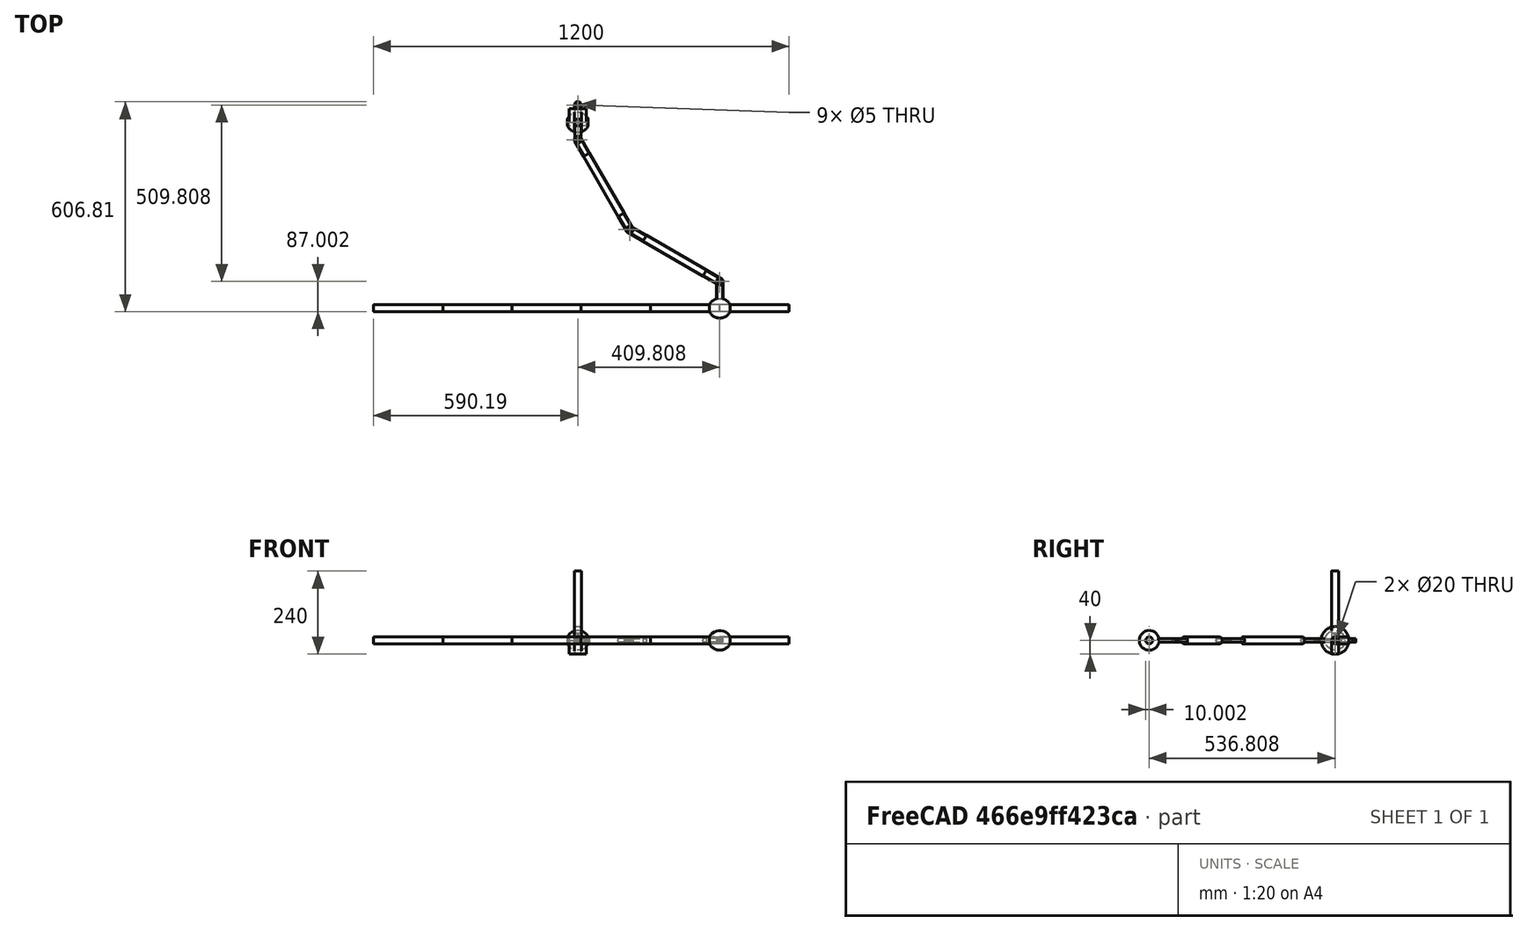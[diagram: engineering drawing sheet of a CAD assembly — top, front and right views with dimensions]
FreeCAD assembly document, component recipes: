
FREECAD ASSEMBLY — COMPONENT RECIPES ("Demo7Rigid")

This assembly document has 7 components, labeled P0..P6 below (a component is one placed body or linked part). 7 of them carry a construction recipe — the FreeCAD feature program that regenerates the part from scratch, quoted from this document or its linked companion documents; the rest are supplied as boundary geometry only. No exploded tour is included for this assembly.
COMPONENT P0 — recipe-attached ("Weight", modeled in this document).
Construction recipe (the document's own serialized feature program — sketch geometry with constraints, then the solid features built on it; lengths are millimeters unless a unit is written):

FEATURE [Sketcher::SketchObject] Sketch
  FullyConstrained = true
  MapMode = 5
  Support = -> [XY_Plane]
  sketch-geometry (2):
    g0: LineSegment StartX=-30 StartY=10 StartZ=0 EndX=30 EndY=10 EndZ=0
    g1: ArcOfCircle CenterX=0 CenterY=-5 CenterZ=0 NormalX=0 NormalY=0 NormalZ=1 AngleXU=0 Radius=33.541 StartAngle=0.463648 EndAngle=2.67795
  constraints (7):
    c: Horizontal(g0)
    c: DistanceY(g-1,g0) = 10
    c: DistanceX(g-1,g0) = 30
    c: PointOnObject(g1,g-2)
    c: DistanceY(g1,g-1) = 5
    c: Coincident(g1,g0)
    c: Coincident(g1,g0)
FEATURE [PartDesign::Revolution] Revolution
  Angle = 360
  Axis = (1,0,0)
  Base = (0,0,0)
  Profile = -> Sketch
  ReferenceAxis = -> Sketch [H_Axis]
FEATURE [PartDesign::CoordinateSystem] WeightTop
  AttacherType = Attacher::AttachEngine3D
  MapMode = 11
  Placement = pos=(30,-1.8e-15,0) rot=(0.707107,0,0.707107;3.14159rad)
  Support = -> [Revolution]
FEATURE [PartDesign::CoordinateSystem] WeightBot
  AttacherType = Attacher::AttachEngine3D
  MapMode = 11
  Placement = pos=(-30,0,0) rot=(0.707107,0,0.707107;3.14159rad)
  Support = -> [Revolution]
FEATURE [PartDesign::CoordinateSystem] WeightLCS
  AttacherType = Attacher::AttachEngine3D
  MapMode = 2
  Support = -> [Body003]
FEATURE [PartDesign::Body] Body  label="Weight"
  Group = -> [Sketch,Revolution,WeightLCS,WeightTop,WeightBot]
  Origin = -> Origin
  Tip = -> Revolution
COMPONENT P1 — recipe-attached ("Rod", modeled in this document).
Construction recipe (the document's own serialized feature program — sketch geometry with constraints, then the solid features built on it; lengths are millimeters unless a unit is written):

FEATURE [Sketcher::SketchObject] Sketch001
  FullyConstrained = true
  MapMode = 5
  Support = -> [XY_Plane001]
  sketch-geometry (1):
    g0: Circle CenterX=0 CenterY=0 CenterZ=0 NormalX=0 NormalY=0 NormalZ=1 AngleXU=0 Radius=10
  constraints (2):
    c: Coincident(g0,g-1)
    c: Diameter(g0) = 20
FEATURE [PartDesign::Pad] Pad
  Direction = (0,0,1)
  Length = 200
  Length2 = 10
  Profile = -> Sketch001
  ReferenceAxis = -> Sketch001 [N_Axis]
  Type = 0
FEATURE [PartDesign::CoordinateSystem] RodTop
  AttacherType = Attacher::AttachEngine3D
  MapMode = 11
  Placement = pos=(0,0,200) rot=(0,0,1;1.5708rad)
  Support = -> [Pad]
FEATURE [PartDesign::CoordinateSystem] RodBottom
  AttacherType = Attacher::AttachEngine3D
  MapMode = 11
  Placement = pos=(0,0,0) rot=(0,0,1;1.5708rad)
  Support = -> [Pad]
FEATURE [PartDesign::Body] Body001  label="Rod"
  Group = -> [Sketch001,Pad,RodTop,RodBottom]
  Origin = -> Origin001
  Tip = -> Pad
COMPONENT P2 — recipe-attached ("LugBody", modeled in this document).
Construction recipe (the document's own serialized feature program — sketch geometry with constraints, then the solid features built on it; lengths are millimeters unless a unit is written):

FEATURE [Sketcher::SketchObject] Sketch002
  FullyConstrained = true
  MapMode = 5
  Support = -> [XY_Plane002]
  sketch-geometry (5):
    g0: LineSegment StartX=-10 StartY=0 StartZ=0 EndX=-10 EndY=50 EndZ=0
    g1: ArcOfCircle CenterX=0 CenterY=50 CenterZ=0 NormalX=0 NormalY=0 NormalZ=1 AngleXU=0 Radius=10 StartAngle=1e-16 EndAngle=3.14159
    g2: LineSegment StartX=10 StartY=50 StartZ=0 EndX=10 EndY=0 EndZ=0
    g3: LineSegment StartX=10 StartY=0 StartZ=0 EndX=-10 EndY=0 EndZ=0
    g4: Circle CenterX=0 CenterY=50 CenterZ=0 NormalX=0 NormalY=0 NormalZ=1 AngleXU=0 Radius=2.5
  constraints (13):
    c: PointOnObject(g0,g-1)
    c: Vertical(g0)
    c: Tangent(g0,g1) = 1.5708
    c: Tangent(g1,g2) = 1.5708
    c: Coincident(g2,g3)
    c: Coincident(g3,g0)
    c: Horizontal(g3)
    c: PointOnObject(g1,g-2)
    c: Vertical(g2)
    c: Diameter(g1) = 20
    c: Distance(g2) = 50
    c: Coincident(g4,g1)
    c: Diameter(g4) = 5
FEATURE [PartDesign::Pad] Pad001
  Direction = (0,0,1)
  Length = 10
  Length2 = 10
  Midplane = true
  Profile = -> Sketch002
  ReferenceAxis = -> Sketch002 [N_Axis]
  Type = 0
FEATURE [PartDesign::Body] Body002  label="LugBody"
  Group = -> [Sketch002,Pad001]
  Origin = -> Origin002
  Tip = -> Pad001
COMPONENT P3 — recipe-attached ("LugCylinder", modeled in this document).
Construction recipe (the document's own serialized feature program — sketch geometry with constraints, then the solid features built on it; lengths are millimeters unless a unit is written):

FEATURE [Sketcher::SketchObject] Sketch003
  FullyConstrained = true
  MapMode = 5
  Placement = pos=(0,0,0) rot=(1,0,0;1.5708rad)
  Support = -> [XZ_Plane003]
  sketch-geometry (1):
    g0: Circle CenterX=0 CenterY=0 CenterZ=0 NormalX=0 NormalY=0 NormalZ=1 AngleXU=0 Radius=10
  constraints (2):
    c: Coincident(g0,g-1)
    c: Diameter(g0) = 20
FEATURE [PartDesign::Pad] Pad002
  Direction = (0,-1,-2e-16)
  Length = 60
  Length2 = 10
  Placement = pos=(0,0,0) rot=(1,0,0;1.5708rad)
  Profile = -> Sketch003
  ReferenceAxis = -> Sketch003 [N_Axis]
  Reversed = true
  Type = 0
FEATURE [PartDesign::Boolean] Boolean
  BaseFeature = -> Pad002
  Group = -> [Body002]
  Type = 2
FEATURE [PartDesign::CoordinateSystem] LugHole
  AttacherType = Attacher::AttachEngine3D
  MapMode = 11
  Placement = pos=(0,50,5) rot=(0,0,1;1.5708rad)
  Support = -> [Boolean]
FEATURE [PartDesign::CoordinateSystem] LugFace
  AttacherType = Attacher::AttachEngine3D
  MapMode = 5
  Placement = pos=(0,0,0) rot=(1,0,0;1.5708rad)
  Support = -> [Boolean]
FEATURE [PartDesign::CoordinateSystem] LugRot30
  AttacherType = Attacher::AttachEngine3D
  AttachmentOffset = pos=(0,0,0) rot=(0,0,1;0.523599rad)
  MapMode = 11
  Placement = pos=(0,50,5) rot=(0,0,1;2.0944rad)
  Support = -> [Boolean]
FEATURE [PartDesign::CoordinateSystem] LugRot60
  AttacherType = Attacher::AttachEngine3D
  AttachmentOffset = pos=(0,0,0) rot=(0,0,1;1.0472rad)
  MapMode = 11
  Placement = pos=(0,50,5) rot=(0,0,1;2.61799rad)
  Support = -> [Boolean]
FEATURE [PartDesign::Body] Body003  label="LugCylinder"
  Group = -> [Sketch003,Pad002,Boolean,LugHole,LugFace,LugRot30,LugRot60]
  Origin = -> Origin003
  Tip = -> Boolean
COMPONENT P4 — recipe-attached ("BobBody", modeled in this document).
Construction recipe (the document's own serialized feature program — sketch geometry with constraints, then the solid features built on it; lengths are millimeters unless a unit is written):

FEATURE [Sketcher::SketchObject] Sketch004
  FullyConstrained = true
  MapMode = 5
  Support = -> [XY_Plane004]
  sketch-geometry (4):
    g0: LineSegment StartX=-10 StartY=0 StartZ=0 EndX=-10 EndY=30 EndZ=0
    g1: ArcOfCircle CenterX=0 CenterY=30 CenterZ=0 NormalX=0 NormalY=0 NormalZ=1 AngleXU=0 Radius=10 StartAngle=2e-16 EndAngle=3.14159
    g2: LineSegment StartX=10 StartY=30 StartZ=0 EndX=10 EndY=0 EndZ=0
    g3: LineSegment StartX=10 StartY=0 StartZ=0 EndX=-10 EndY=0 EndZ=0
  constraints (11):
    c: PointOnObject(g0,g-1)
    c: Vertical(g0)
    c: Tangent(g0,g1) = 1.5708
    c: Tangent(g1,g2) = 1.5708
    c: Coincident(g2,g3)
    c: Coincident(g3,g0)
    c: Vertical(g2)
    c: PointOnObject(g1,g-2)
    c: Diameter(g1) = 20
    c: Distance(g0) = 30
    c: PointOnObject(g2,g-1)
FEATURE [PartDesign::Revolution] Revolution001
  Angle = 360
  Axis = (1,0,0)
  Base = (0,0,0)
  Profile = -> Sketch004
  ReferenceAxis = -> Sketch004 [H_Axis]
FEATURE [PartDesign::CoordinateSystem] BobBody  label="BobBody001"
  AttacherType = Attacher::AttachEngine3D
  MapMode = 11
  Placement = pos=(-10,0,0) rot=(0.707107,0,0.707107;3.14159rad)
  Support = -> [Revolution001]
FEATURE [PartDesign::Body] Body004  label="BobBody"
  Group = -> [Sketch004,Revolution001,BobBody]
  Origin = -> Origin004
  Tip = -> Revolution001
COMPONENT P5 — recipe-attached ("GroundBody", modeled in this document).
Construction recipe (the document's own serialized feature program — sketch geometry with constraints, then the solid features built on it; lengths are millimeters unless a unit is written):

FEATURE [Sketcher::SketchObject] Sketch005
  FullyConstrained = true
  MapMode = 5
  Support = -> [XY_Plane005]
  sketch-geometry (4):
    g0: LineSegment StartX=-25 StartY=10 StartZ=0 EndX=25 EndY=10 EndZ=0
    g1: LineSegment StartX=25 StartY=10 StartZ=0 EndX=25 EndY=-10 EndZ=0
    g2: LineSegment StartX=25 StartY=-10 StartZ=0 EndX=-25 EndY=-10 EndZ=0
    g3: LineSegment StartX=-25 StartY=-10 StartZ=0 EndX=-25 EndY=10 EndZ=0
  constraints (11):
    c: Coincident(g0,g1)
    c: Coincident(g1,g2)
    c: Coincident(g2,g3)
    c: Coincident(g3,g0)
    c: Horizontal(g0)
    c: Horizontal(g2)
    c: Vertical(g1)
    c: Vertical(g3)
    c: DistanceY(g2,g0) = 20
    c: DistanceX(g0,g0) = 50
    c: Symmetric(g0,g1,g-1)
FEATURE [PartDesign::Pad] Pad003
  Direction = (0,0,1)
  Length = 40
  Length2 = 10
  Profile = -> Sketch005
  ReferenceAxis = -> Sketch005 [N_Axis]
  Reversed = true
  Type = 0
FEATURE [PartDesign::CoordinateSystem] GroundLCS
  AttacherType = Attacher::AttachEngine3D
  MapMode = 5
  Placement = pos=(0,0,-40) rot=(1,0,0;3.14159rad)
  Support = -> [Pad003]
FEATURE [PartDesign::Body] Body005  label="GroundBody"
  Group = -> [Sketch005,Pad003,GroundLCS]
  Origin = -> Origin005
  Tip = -> Pad003
COMPONENT P6 — recipe-attached ("Spacer", modeled in this document).
Construction recipe (the document's own serialized feature program — sketch geometry with constraints, then the solid features built on it; lengths are millimeters unless a unit is written):

FEATURE [Sketcher::SketchObject] Sketch006
  FullyConstrained = true
  MapMode = 5
  Support = -> [XY_Plane007]
  sketch-geometry (2):
    g0: Circle CenterX=0 CenterY=0 CenterZ=0 NormalX=0 NormalY=0 NormalZ=1 AngleXU=0 Radius=10
    g1: Circle CenterX=0 CenterY=0 CenterZ=0 NormalX=0 NormalY=0 NormalZ=1 AngleXU=0 Radius=2.5
  constraints (4):
    c: Coincident(g0,g-1)
    c: Coincident(g1,g0)
    c: Diameter(g0) = 20
    c: Diameter(g1) = 5
FEATURE [PartDesign::Pad] Pad004
  Direction = (0,0,1)
  Length = 20
  Length2 = 10
  Profile = -> Sketch006
  ReferenceAxis = -> Sketch006 [N_Axis]
  Type = 0
FEATURE [PartDesign::CoordinateSystem] SpacerTop
  AttacherType = Attacher::AttachEngine3D
  MapMode = 11
  Placement = pos=(0,0,20) rot=(0,0,1;1.5708rad)
  Support = -> [Pad004]
FEATURE [PartDesign::Body] Body006  label="Spacer"
  Group = -> [Sketch006,Pad004,SpacerTop]
  Origin = -> Origin007
  Tip = -> Pad004
PROVENANCE & LICENSES
A FreeCAD (.FCStd) document from a public repository crawl; recipes are the document's own serialized feature recipes (and, for linked parts, companion documents' recipes).
License: gpl-3.0.
